# Revit family: 2CKA001713A0202
name_source: partatom
category: Elektroinstallationen
revit_build: Autodesk Revit 2017 (Build: 20160225_1515(x64)
units: mm (PartAtom-declared; Revit-internal decimal feet)

## family parameters
Basisbauteil = Fläche
Beim Laden mit Abzugskörper schneiden = Nein
Bemaßung runder Anschluss = Durchmesser verwenden
Beschriftungsausrichtung beibehalten = Ja
Gemeinsam genutzt = Nein
Raumberechnungspunkt = Nein
Teiletyp = Normal

## types (1)
- 2CKA001713A0202
    Aufdruck/Kennzeichnung = Symbol "Pfeile"
    Ausführung = zweiteilige Wippe
    Ausführung der Oberfläche = glänzend
    BIM = https://media.live.bim.site
    BIMSITE_PRODUCT_ID = 091958876bd64128a51eb7b8eec31ab17e587757
    Befestigungsart = Klemmbefestigung
    Beschreibung = Wippe, alpinweiß, Busch-balance SI, Bedienelemente für Jalousiesteuerung/Zeitschaltuhren, Wippe mit Aufdruck Als Abdeckung für UP-Jalousieschalter/-taster. Für Einsatz 2000/4 und 2020/4 US.
    Datenblatt = https://media.live.bim.site
    Farbe = weiß
    GTIN = 4011395190463
    Geeignet für Schutzart (IP) = IP20
    Gerätebreite [mm] = 55
    Gerätehöhe [mm] = 55
    Gerätetiefe [mm] = 11
    HAN = 2CKA001713A0202
    Halogenfrei = Ja
    HeinzeBIM = https://www.heinze.de
    Hersteller = Busch-Jaeger Elektro GmbH
    Ist System = Nein
    Ist Zubehör = Nein
    Oberfläche = unbehandelt
    Produktseite = https://media.live.bim.site
    RAL-Nummer (ähnlich) = 9010
    TYPE = 2504-914
    Typname = Wippe, alpinweiß, Busch-balance SI, Bedienelemente für Jalousiesteuerung/Zeitschaltuhren
    Verwendung = Jalousie
    Vorgabe-Ansicht = 1219 mm
    Werkstoff = Kunststoff
    Werkstoffgüte = Thermoplast
    White = Whitte

## geometry (parser evidence)
native form markers: Sweep x2
no freeform markers — native parametric forms only
